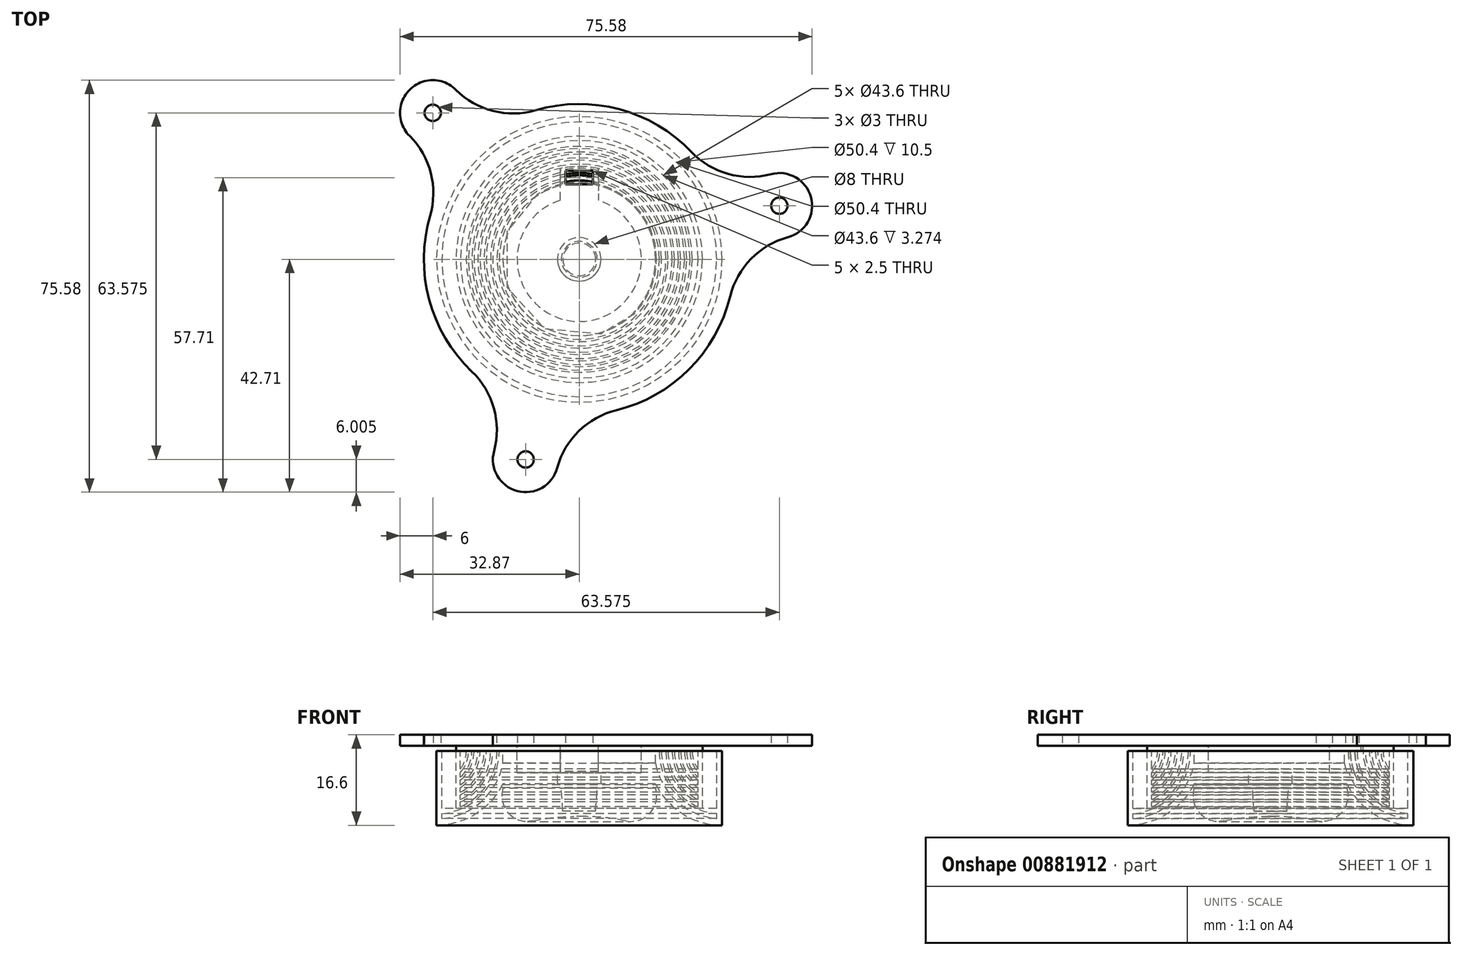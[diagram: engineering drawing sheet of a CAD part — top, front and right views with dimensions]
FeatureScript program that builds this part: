
annotation { "Feature Type Name" : "Feature", "Feature Type Description" : "" }
export const myFeature = defineFeature(function(context is Context, id is Id, definition is map)
    precondition{}
    {
        {
            var Q0;
            Q0=qCreatedBy(makeId("Top.planeOp"),FACE);
            var sketch = newSketch(context, id + "F0", { "sketchPlane" : qUnion([Q0])});
            skCircle(sketch, "E0", {"center": v(0, 0) * mm, "radius": 28.5 * mm});
            skCircle(sketch, "E1", {"center": v(-26.87, 26.87) * mm, "radius": 1.5 * mm});
            skLineSegment(sketch, "E2", {"start": v(0, 0) * mm, "end": v(-26.87, 26.87) * mm, "construction": true});
            skCircle(sketch, "E3", {"center": v(0, 0) * mm, "radius": 27 * mm, "construction": true});
            skLineSegment(sketch, "E4", {"start": v(-0.08, 0) * mm, "end": v(27, 0) * mm, "construction": true});
            skArc(sketch, "E5", {"start": v(-22.63, 31.11) * mm, "mid": v(-31.11, 31.11) * mm, "end": v(-31.11, 22.63) * mm});
            skArc(sketch, "E6", {"start": v(-27.36, 7.98) * mm, "mid": v(-27.23, 15.82) * mm, "end": v(-31.11, 22.63) * mm});
            skLineSegment(sketch, "E7", {"start": v(-31.11, 22.63) * mm, "end": v(-22.63, 31.11) * mm, "construction": true});
            skArc(sketch, "E8.MirrorCS", {"start": v(-7.98, 27.36) * mm, "mid": v(-15.82, 27.23) * mm, "end": v(-22.63, 31.11) * mm});
            skPoint(sketch, "E9.1.0", {"position": v(-9.84, -36.7) * mm});
            skArc(sketch, "E9.1.1", {"start": v(6.77, -27.68) * mm, "mid": v(-0.08, -31.5) * mm, "end": v(-4.04, -38.26) * mm});
            skArc(sketch, "E9.1.2", {"start": v(-15.63, -35.15) * mm, "mid": v(-11.39, -42.5) * mm, "end": v(-4.04, -38.26) * mm});
            skArc(sketch, "E9.1.3", {"start": v(-19.7, -20.6) * mm, "mid": v(-15.67, -27.31) * mm, "end": v(-15.63, -35.15) * mm});
            skLineSegment(sketch, "E9.1.5", {"start": v(0, 0) * mm, "end": v(-9.84, -36.7) * mm, "construction": true});
            skLineSegment(sketch, "E9.1.8", {"start": v(-4.04, -38.26) * mm, "end": v(-15.63, -35.15) * mm, "construction": true});
            skCircle(sketch, "E9.1.9", {"center": v(-9.84, -36.7) * mm, "radius": 1.5 * mm});
            skPoint(sketch, "E9.2.0", {"position": v(36.7, 9.84) * mm});
            skArc(sketch, "E9.2.1", {"start": v(20.6, 19.7) * mm, "mid": v(27.31, 15.67) * mm, "end": v(35.15, 15.63) * mm});
            skArc(sketch, "E9.2.2", {"start": v(38.26, 4.04) * mm, "mid": v(42.5, 11.39) * mm, "end": v(35.15, 15.63) * mm});
            skArc(sketch, "E9.2.3", {"start": v(27.68, -6.77) * mm, "mid": v(31.5, 0.08) * mm, "end": v(38.26, 4.04) * mm});
            skLineSegment(sketch, "E9.2.5", {"start": v(0, 0) * mm, "end": v(36.7, 9.84) * mm, "construction": true});
            skLineSegment(sketch, "E9.2.8", {"start": v(35.15, 15.63) * mm, "end": v(38.26, 4.04) * mm, "construction": true});
            skCircle(sketch, "E9.2.9", {"center": v(36.7, 9.84) * mm, "radius": 1.5 * mm});
            skSolve(sketch);
        }
        {
            var Q0;
            Q0 = qSketchRegion(id + "F0", true);
            extrude(context, id + "F1", {"entities" : qUnion([Q0]), "depth" : 2 * mm, "offsetDistance" : 25 * mm});
        }
        {
            var Q0;
            Q0=qCreatedBy(makeId("Top.planeOp"),FACE);
            var sketch = newSketch(context, id + "F2", { "sketchPlane" : qUnion([Q0])});
            skLineSegment(sketch, "E10.bottom", {"start": v(6, -6) * mm, "end": v(-6, -6) * mm, "construction": true});
            skLineSegment(sketch, "E10.top", {"start": v(6, 6) * mm, "end": v(-6, 6) * mm, "construction": true});
            skLineSegment(sketch, "E10.left", {"start": v(6, -6) * mm, "end": v(6, 6) * mm, "construction": true});
            skLineSegment(sketch, "E10.right", {"start": v(-6, -6) * mm, "end": v(-6, 6) * mm, "construction": true});
            skPoint(sketch, "E10.middle", {"position": v(0, 0) * mm});
            skCircle(sketch, "E11", {"center": v(0, 0) * mm, "radius": 3.25 * mm, "construction": true});
            skLineSegment(sketch, "E12.left", {"start": v(2.5, -11) * mm, "end": v(2.5, -6) * mm, "construction": true});
            skLineSegment(sketch, "E12.right", {"start": v(-2.5, -11) * mm, "end": v(-2.5, -6) * mm, "construction": true});
            skLineSegment(sketch, "E13.trimOffspring", {"start": v(-2.5, 6) * mm, "end": v(-2.5, 11) * mm, "construction": true});
            skLineSegment(sketch, "E14.trimOffspring", {"start": v(2.5, 6) * mm, "end": v(2.5, 11) * mm, "construction": true});
            skLineSegment(sketch, "E15.0", {"start": v(6.4, 6.4) * mm, "end": v(4, 6.4) * mm});
            skLineSegment(sketch, "E15.1", {"start": v(6.4, -6.4) * mm, "end": v(6.4, 6.4) * mm});
            skLineSegment(sketch, "E15.2", {"start": v(6.4, -6.4) * mm, "end": v(4, -6.4) * mm});
            skLineSegment(sketch, "E15.3", {"start": v(-6.4, -6.4) * mm, "end": v(-6.4, 6.4) * mm});
            skArc(sketch, "E16", {"start": v(-4, 10.25) * mm, "mid": v(-11, 0) * mm, "end": v(-4, -10.25) * mm});
            skLineSegment(sketch, "E17.left", {"start": v(4, 10.25) * mm, "end": v(4, 6.4) * mm});
            skLineSegment(sketch, "E17.right", {"start": v(-4, 10.25) * mm, "end": v(-4, 6.4) * mm});
            skLineSegment(sketch, "E18.trimOffspring", {"start": v(4, -6.4) * mm, "end": v(4, -10.25) * mm});
            skLineSegment(sketch, "E19.trimOffspring", {"start": v(-4, -6.4) * mm, "end": v(-4, -10.25) * mm});
            skLineSegment(sketch, "E20.trimOffspring", {"start": v(-4, 6.4) * mm, "end": v(-6.4, 6.4) * mm});
            skLineSegment(sketch, "E21.trimOffspring", {"start": v(-4, -6.4) * mm, "end": v(-6.4, -6.4) * mm});
            skArc(sketch, "E22.trimOffspring", {"start": v(4, -10.25) * mm, "mid": v(11, 0) * mm, "end": v(4, 10.25) * mm});
            skLineSegment(sketch, "E23.bottom", {"start": v(2.5, 13.75) * mm, "end": v(-2.5, 13.75) * mm});
            skLineSegment(sketch, "E23.top", {"start": v(2.5, 16.25) * mm, "end": v(-2.5, 16.25) * mm});
            skLineSegment(sketch, "E23.left", {"start": v(2.5, 13.75) * mm, "end": v(2.5, 16.25) * mm});
            skLineSegment(sketch, "E23.right", {"start": v(-2.5, 13.75) * mm, "end": v(-2.5, 16.25) * mm});
            skPoint(sketch, "E23.middle", {"position": v(0, 15) * mm});
            skLineSegment(sketch, "E24", {"start": v(-3.25, 0) * mm, "end": v(3.25, 0) * mm, "construction": true});
            skLineSegment(sketch, "E25", {"start": v(0, 3.25) * mm, "end": v(0, -3.25) * mm, "construction": true});
            skCircle(sketch, "E26.0", {"center": v(0, 0) * mm, "radius": 24.5 * mm, "construction": true});
            skCircle(sketch, "E27.0", {"center": v(0, 0) * mm, "radius": 27 * mm, "construction": true});
            skSolve(sketch);
        }
        {
            var Q0;
            Q0=makeQuery(id+"F2.imprint","IMPRINT",FACE,{"disambiguationData":[TD([[makeQuery(id+"F2.imprint","IMPRINT",EDGE,{"derivedFrom":sQuery(id+"F2.wireOp",EDGE,"E15.3")}),1.0]])]});
            var Q1;
            Q1=makeQuery(id+"F2.imprint","IMPRINT",FACE,{"disambiguationData":[TD([[makeQuery(id+"F2.imprint","IMPRINT",EDGE,{"derivedFrom":sQuery(id+"F2.wireOp",EDGE,"E15.0")}),-1.0]])]});
            extrude(context, id + "F3", {"entities" : qUnion([Q0, Q1]), "operationType" : NewBodyOperationType.ADD, "oppositeDirection" : true, "depth" : 4 * mm, "offsetDistance" : 25 * mm});
        }
        {
            var Q0;
            Q0=makeQuery(id+"F2.imprint","IMPRINT",FACE,{"disambiguationData":[TD([[makeQuery(id+"F2.imprint","IMPRINT",EDGE,{"derivedFrom":sQuery(id+"F2.wireOp",EDGE,"E23.bottom")}),-1.0]])]});
            var Q1;
            Q1=makeQuery(id+"F2.imprint","IMPRINT",FACE,{"disambiguationData":[TD([[makeQuery(id+"F2.imprint","IMPRINT",EDGE,{"derivedFrom":sQuery(id+"F2.wireOp",EDGE,"fcf4720d-162a-46d9-bce0-dd81c167c90f0.MirrorCS")}),-1.0]])]});
            extrude(context, id + "F4", {"entities" : qUnion([Q0, Q1]), "operationType" : NewBodyOperationType.REMOVE, "endBound" : BoundingType.THROUGH_ALL, "depth" : 25 * mm, "offsetDistance" : 25 * mm});
        }
        {
            var Q0;
            Q0=qCreatedBy(makeId("Front.planeOp"),FACE);
            var sketch = newSketch(context, id + "F5", { "sketchPlane" : qUnion([Q0])});
            skLineSegment(sketch, "E28.2", {"start": v(14, 0) * mm, "end": v(22.6, 0) * mm});
            skLineSegment(sketch, "E29", {"start": v(26.2, -11.5) * mm, "end": v(26.2, -14.6) * mm});
            skLineSegment(sketch, "E30", {"start": v(14, 0) * mm, "end": v(4, 0) * mm});
            skLineSegment(sketch, "E31", {"start": v(0, 0) * mm, "end": v(0, -7) * mm, "construction": true});
            skLineSegment(sketch, "E32", {"start": v(14, 0) * mm, "end": v(14, -7) * mm, "construction": true});
            skLineSegment(sketch, "E33", {"start": v(14, -7) * mm, "end": v(4, -7) * mm});
            skLineSegment(sketch, "E34", {"start": v(4, -7) * mm, "end": v(4, 0) * mm});
            skArc(sketch, "E35", {"start": v(14, -7) * mm, "mid": v(19.01, -12.54) * mm, "end": v(26.2, -14.6) * mm});
            skLineSegment(sketch, "E36", {"start": v(26.2, -1) * mm, "end": v(26.2, -11.5) * mm});
            skArc(sketch, "E37.0", {"start": v(13.44, 0) * mm, "mid": v(16.8, -9.69) * mm, "end": v(26.2, -13.8) * mm});
            skLineSegment(sketch, "E38.0", {"start": v(25.2, -1) * mm, "end": v(25.2, -11.5) * mm});
            skLineSegment(sketch, "E39", {"start": v(25.2, -11.5) * mm, "end": v(22.6, -11.5) * mm});
            skLineSegment(sketch, "E40", {"start": v(22.6, -11.5) * mm, "end": v(22.6, 0) * mm});
            skLineSegment(sketch, "E41", {"start": v(25.2, -1) * mm, "end": v(26.2, -1) * mm});
            skArc(sketch, "E42.0", {"start": v(14, -3.2) * mm, "mid": v(17.87, -10.18) * mm, "end": v(25.2, -13.36) * mm});
            skLineSegment(sketch, "E43", {"start": v(22.6, 0) * mm, "end": v(26.2, 0) * mm, "construction": true});
            skLineSegment(sketch, "E44", {"start": v(26.2, 0) * mm, "end": v(26.2, -1) * mm, "construction": true});
            skArc(sketch, "E45", {"start": v(25.2, -12.48) * mm, "mid": v(17.7, -8.79) * mm, "end": v(14.68, -1) * mm});
            skArc(sketch, "E46", {"start": v(15.08, -1) * mm, "mid": v(16.9, -7.11) * mm, "end": v(21.8, -11.21) * mm});
            skArc(sketch, "E47", {"start": v(21.8, -10.34) * mm, "mid": v(17.48, -6.53) * mm, "end": v(15.88, -1) * mm});
            skArc(sketch, "E48", {"start": v(21.8, -9.9) * mm, "mid": v(17.77, -6.23) * mm, "end": v(16.28, -1) * mm});
            skArc(sketch, "E49", {"start": v(17.06, -1) * mm, "mid": v(18.33, -5.66) * mm, "end": v(21.8, -9.01) * mm});
            skArc(sketch, "E50", {"start": v(17.46, -1) * mm, "mid": v(18.62, -5.36) * mm, "end": v(21.8, -8.56) * mm});
            skArc(sketch, "E51", {"start": v(18.2, -1) * mm, "mid": v(19.16, -4.8) * mm, "end": v(21.8, -7.68) * mm});
            skLineSegment(sketch, "E52", {"start": v(25.2, -12.48) * mm, "end": v(25.2, -13.36) * mm});
            skLineSegment(sketch, "E53", {"start": v(21.8, -11.21) * mm, "end": v(21.8, -10.34) * mm});
            skLineSegment(sketch, "E54", {"start": v(21.8, -9.9) * mm, "end": v(21.8, -9.01) * mm});
            skLineSegment(sketch, "E55", {"start": v(14, -3.2) * mm, "end": v(14, -1) * mm});
            skLineSegment(sketch, "E56", {"start": v(14, -1) * mm, "end": v(14.68, -1) * mm});
            skLineSegment(sketch, "E57", {"start": v(21.8, -8.56) * mm, "end": v(21.8, -7.68) * mm});
            skLineSegment(sketch, "E58", {"start": v(18.2, -1) * mm, "end": v(17.46, -1) * mm});
            skLineSegment(sketch, "E59", {"start": v(17.06, -1) * mm, "end": v(16.28, -1) * mm});
            skLineSegment(sketch, "E60", {"start": v(15.88, -1) * mm, "end": v(15.08, -1) * mm});
            skLineSegment(sketch, "E61", {"start": v(14.68, -1) * mm, "end": v(15.08, -1) * mm, "construction": true});
            skLineSegment(sketch, "E62", {"start": v(15.88, -1) * mm, "end": v(16.28, -1) * mm, "construction": true});
            skLineSegment(sketch, "E63", {"start": v(17.06, -1) * mm, "end": v(17.46, -1) * mm, "construction": true});
            skArc(sketch, "E64", {"start": v(21.8, -7.2) * mm, "mid": v(19.45, -4.48) * mm, "end": v(18.6, -1) * mm});
            skLineSegment(sketch, "E65", {"start": v(18.2, -1) * mm, "end": v(18.6, -1) * mm, "construction": true});
            skArc(sketch, "E66", {"start": v(21.8, -6.32) * mm, "mid": v(19.96, -3.94) * mm, "end": v(19.3, -1) * mm});
            skArc(sketch, "E67", {"start": v(21.8, -5.79) * mm, "mid": v(20.25, -3.61) * mm, "end": v(19.7, -1) * mm});
            skArc(sketch, "E68", {"start": v(21.8, -4.9) * mm, "mid": v(20.7, -3.1) * mm, "end": v(20.32, -1) * mm});
            skLineSegment(sketch, "E69", {"start": v(21.8, -4.9) * mm, "end": v(21.8, -5.79) * mm});
            skLineSegment(sketch, "E70", {"start": v(21.8, -6.32) * mm, "end": v(21.8, -7.2) * mm});
            skLineSegment(sketch, "E71", {"start": v(20.32, -1) * mm, "end": v(19.7, -1) * mm});
            skLineSegment(sketch, "E72", {"start": v(19.3, -1) * mm, "end": v(18.6, -1) * mm});
            skLineSegment(sketch, "E73", {"start": v(19.3, -1) * mm, "end": v(19.7, -1) * mm});
            skArc(sketch, "E74", {"start": v(21.8, -4.27) * mm, "mid": v(21, -2.72) * mm, "end": v(20.72, -1) * mm});
            skLineSegment(sketch, "E75", {"start": v(20.72, -1) * mm, "end": v(21.8, -1) * mm});
            skLineSegment(sketch, "E76", {"start": v(21.8, -1) * mm, "end": v(21.8, -4.27) * mm});
            skLineSegment(sketch, "E77", {"start": v(20.32, -1) * mm, "end": v(20.72, -1) * mm, "construction": true});
            skSolve(sketch);
        }
        {
            var Q0;
            Q0 = qSketchRegion(id + "F5", true);
            var Q1;
            Q1=sQuery(id+"F5.wireOp",EDGE,"E31");
            revolve(context, id + "F6", {"surfaceOperationType" : NewSurfaceOperationType.NEW, "entities" : qUnion([Q0]), "axis" : qUnion([Q1]), "revolveType" : RevolveType.FULL});
        }
        {
            var Q0;
            Q0=makeQuery(id+"F1.opExtrude","CAP_FACE",FACE,{"disambiguationData":[OSD([sQuery(id+"F0.wireOp",EDGE,"E0"),sQuery(id+"F0.wireOp",EDGE,"4TyHnLzo-Rsoi-rGjR-wxT6-94tr7AON6tRp"),sQuery(id+"F0.wireOp",EDGE,"dbae1985-7272-4468-829f-d02c33586e02"),sQuery(id+"F0.wireOp",EDGE,"46c23bec-6b31-46ef-a9f7-6be168fb7e93"),sQuery(id+"F0.wireOp",EDGE,"E1"),sQuery(id+"F0.wireOp",EDGE,"5dbe542f-be41-4dfd-9623-7e041be02cc6.1.0"),sQuery(id+"F0.wireOp",EDGE,"5dbe542f-be41-4dfd-9623-7e041be02cc6.1.1"),sQuery(id+"F0.wireOp",EDGE,"5dbe542f-be41-4dfd-9623-7e041be02cc6.1.2"),sQuery(id+"F0.wireOp",EDGE,"5dbe542f-be41-4dfd-9623-7e041be02cc6.1.3"),sQuery(id+"F0.wireOp",EDGE,"5dbe542f-be41-4dfd-9623-7e041be02cc6.2.0"),sQuery(id+"F0.wireOp",EDGE,"5dbe542f-be41-4dfd-9623-7e041be02cc6.2.1"),sQuery(id+"F0.wireOp",EDGE,"5dbe542f-be41-4dfd-9623-7e041be02cc6.2.2"),sQuery(id+"F0.wireOp",EDGE,"5dbe542f-be41-4dfd-9623-7e041be02cc6.2.3")])],"isStart":true});
            var sketch = newSketch(context, id + "F7", { "sketchPlane" : qUnion([Q0])});
            skLineSegment(sketch, "E78", {"start": v(-3.5, -10.85) * mm, "end": v(-3.5, -16.64) * mm});
            skLineSegment(sketch, "E79", {"start": v(3.5, -16.64) * mm, "end": v(3.5, -10.85) * mm});
            skArc(sketch, "E80", {"start": v(3.5, -16.64) * mm, "mid": v(0, -17) * mm, "end": v(-3.5, -16.64) * mm});
            skArc(sketch, "E81", {"start": v(3.5, -10.85) * mm, "mid": v(0, 11.4) * mm, "end": v(-3.5, -10.85) * mm});
            skCircle(sketch, "E82", {"center": v(0, 0) * mm, "radius": 4 * mm});
            skLineSegment(sketch, "E83", {"start": v(-3.5, -10.85) * mm, "end": v(3.5, -10.85) * mm, "construction": true});
            skLineSegment(sketch, "E84", {"start": v(0, 0) * mm, "end": v(0, -10.85) * mm, "construction": true});
            skArc(sketch, "E85.0", {"start": v(4, 10.25) * mm, "mid": v(11, 0) * mm, "end": v(4, -10.25) * mm, "construction": true});
            skSolve(sketch);
        }
        {
            var Q0;
            Q0 = qSketchRegion(id + "F7", true);
            extrude(context, id + "F8", {"entities" : qUnion([Q0]), "operationType" : NewBodyOperationType.REMOVE, "depth" : 5 * mm, "offsetDistance" : 25 * mm});
        }
        {
            var Q0;
            Q0=qCreatedBy(makeId("Front.planeOp"),FACE);
            var sketch = newSketch(context, id + "F9", { "sketchPlane" : qUnion([Q0])});
            skLineSegment(sketch, "E86.bottom", {"start": v(3.3, -7.8) * mm, "end": v(14, -7.8) * mm});
            skLineSegment(sketch, "E87.0", {"start": v(-26.2, -14.6) * mm, "end": v(26.2, -14.6) * mm, "construction": true});
            skLineSegment(sketch, "E88.0", {"start": v(14, -7) * mm, "end": v(4, -7) * mm, "construction": true});
            skLineSegment(sketch, "E89", {"start": v(3, -12) * mm, "end": v(0, -12) * mm});
            skLineSegment(sketch, "E90", {"start": v(3, -12) * mm, "end": v(3.3, -7.8) * mm});
            skPoint(sketch, "E91.visualSharp", {"position": v(8.2, -7.8) * mm});
            skPoint(sketch, "E92.orphan", {"position": v(0, -7.8) * mm});
            skLineSegment(sketch, "E93", {"start": v(0, -13) * mm, "end": v(0, -12) * mm});
            skLineSegment(sketch, "E94", {"start": v(3, -13.8) * mm, "end": v(14, -13.8) * mm, "construction": true});
            skLineSegment(sketch, "E95", {"start": v(0, -13) * mm, "end": v(1, -13) * mm});
            skArc(sketch, "E96", {"start": v(1, -13) * mm, "mid": v(4.77, -13.2) * mm, "end": v(8.5, -13.8) * mm});
            skArc(sketch, "E97", {"start": v(8.5, -13.8) * mm, "mid": v(12.97, -12.37) * mm, "end": v(14, -7.8) * mm});
            skSolve(sketch);
        }
        {
            var Q0;
            Q0=makeQuery(id+"F9.imprint","IMPRINT",FACE,{"disambiguationData":[TD([[makeQuery(id+"F9.imprint","IMPRINT",EDGE,{"derivedFrom":sQuery(id+"F9.wireOp",EDGE,"E86.bottom")}),-1.0]])]});
            var Q1;
            Q1=sQuery(id+"F5.wireOp",EDGE,"E31");
            revolve(context, id + "F10", {"surfaceOperationType" : NewSurfaceOperationType.NEW, "entities" : qUnion([Q0]), "axis" : qUnion([Q1]), "revolveType" : RevolveType.FULL});
        }
    });
